# Revit family: GRAS_HW-52W-K-15-20
name_source: partatom
category: Osprzęt hydrauliczny
revit_build: Autodesk Revit 2018 (Build: 20190510_1515(x64)
units: mm (PartAtom-declared; Revit-internal decimal feet)

## family parameters
Obiekt nadrzędny = Powierzchnia
Punkt obliczania pomieszczeń = Nie
Tnij formami wycięć po wczytaniu = Nie
Typ części = Normalny
Współdzielony = Nie
Wymiar okrągłego złącza = Użyj średnicy

## types (2) — shared parameters
Base_Frame = 22 mm  [stored 0.0721785 ft]
Cabinet_Depth = 180 mm  [stored 0.590551 ft]
Cabinet_H_Width = 550 mm
Cabinet_Height = 600 mm  [stored 1.9685 ft]
Cabinet_Width = 700 mm  [stored 2.29659 ft]
D1 = 100 mm  [stored 0.328084 ft]
DN = 50 mm  [stored 0.164042 ft]
Flow = 246.0 L/s
H1 = 100 mm  [stored 0.328084 ft]
Hole_Depth = 190 mm
Hole_Height = 620 mm
Hole_Width = 720 mm  [stored 2.3622 ft]
K_factor = 42
Model = HW-52W-K-15/20, RAL3000
Opis = http://gras.pl
Partition_H_Width = 500 mm  [stored 1.64042 ft]
Producent = GRAS PPPH
URL = http://www.gras.pl
zero-valued in all types: 0, Domyślna rzędna, Mounting_point, mounting_plane

## per-type parameters (varying)
| type | Cabinet_Material |
| HW-52W-K-15/20, RAL3000 | DC01, RAL3000 |
| HW-52W-K-15/20, RAL9010 | DC01, RAL9010 |

note: [stored X ft] marks values corroborated as IEEE doubles in the binary element streams (Revit-internal decimal feet)

## geometry (parser evidence)
native form markers: Blend x8
no freeform markers — native parametric forms only
